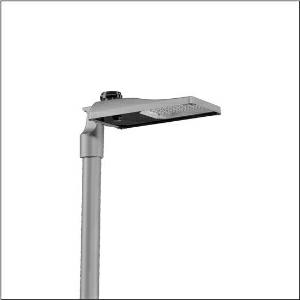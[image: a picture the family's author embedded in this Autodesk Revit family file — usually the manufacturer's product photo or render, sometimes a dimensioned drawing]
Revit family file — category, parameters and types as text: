
# Revit family: streetlight_sl_31_mini___st1_0a_5xh2d35m08ja_015a
name_source: partatom
category: Lighting Fixtures
units: mm (PartAtom-declared; Revit-internal decimal feet)

## family parameters
Cut with Voids When Loaded = No
Host = Face
Light Source = No
Part Type = Normal
Room Calculation Point = No
Round Connector Dimension = Use Diameter
Shared = No

## types (1)
- --- (1 x LED, 12270 lm, 82.5 W, 3000K)
    Apparent Load = 83 VA
    CIE Flux Codes = 40 73 97 100 100
    Color Rendering = 70
    Color Temperature = 3000K
    Default Elevation = 1800 mm
    Description = Streetlight SL 31 mini NEMA (7pin), Desk-Remote mast luminaire for post-top, side-entry; light control with lens of PMMA; light distribution: ST1.0a, direct asymmetric distribution, for standard-compliant lighting for roads and squares; LED: luminous flux: 12.270lm, light colour: 730, colour temperature: 3000K; luminous efficacy: 148,7lm/W; control: pre-setting: linear dimming characteristic, flexible luminous flux parameterisation, time-dependent luminous flux control, constant luminous flux control, intelligent temperature release in ECG and LED module, overheat protection; luminaire housing, of diecast aluminium, Siteco® metallic grey (DB 702S), corrosivity category C5 high according to DIN EN ISO 12944; cover of toughened safety glass, transparent, mast flange of diecast aluminium, Siteco® metallic grey (DB 702S), spigot size: 76/60mm, mast flange included unmounted; with cable H07RN-F 3x 1.5mm², cable length: 10,5m, connection cable pre-assembled; mains connection: 220..240V, AC, 50/60Hz; power consumption (at start of service life): 82,5W / (at end of service life): 90,1W / (with reduced operation 50%): 36,8W; protection rating (complete): IP66; insulation class (complete): insulation class I (protective earthing); impact resistance: IK09; certification: CE, ENEC, ENEC+, VDE, UKCA; permissible operating ambient temperature for outdoor applications: -40..+50°C; packaging unit: 1 piece

Light Distribution: ST1.0a
    Height = 76 mm
    Lamp = 1 x LED
    Lamp Light Flux = 12270 lm
    Lamp Power = 82.5 W
    Lamp count = 1
    Length = 547 mm
    Luminous efficacy = 149 lm/W
    Manufacturer = Siteco
    ModVariant = No
    Model = 5XH2D35M08JA
    Number of Poles = 1
    OnlyDefault = Yes
    Power Factor = 1
    Product Name = Streetlight SL 31 mini | ST1.0a
    Product group = mast luminaire | pylon top
    ProductGroupID = 6100
    Protection Class = Protection class I
    Protection Degree = IP 66
    RLX_Detail_Level = 1
    RLX_Emergency_Light_Flux = 0 lm
    RLX_Emergency_Type = 0
    RLX_Emergency_Type_DB = No
    RlxData = <blob elided: 40313 chars, md5=219536a9>
    Socket = socket
    Standby Power = 0 W
    System Light Flux = 12270 lm
    System Power = 83 W
    Type Comments = factory setting: luminous flux: 100 % | dim-lin: 254 | 870 mA
    Type Image = l_1300324.jpg
    URL = http://relux.com
    VarID = @adj_050606
    Voltage = 0 V
    Weight = 0.00 kg
    Width = 265 mm

## geometry (parser evidence)
native form markers: Blend x4, Sweep x10
no freeform markers — native parametric forms only
